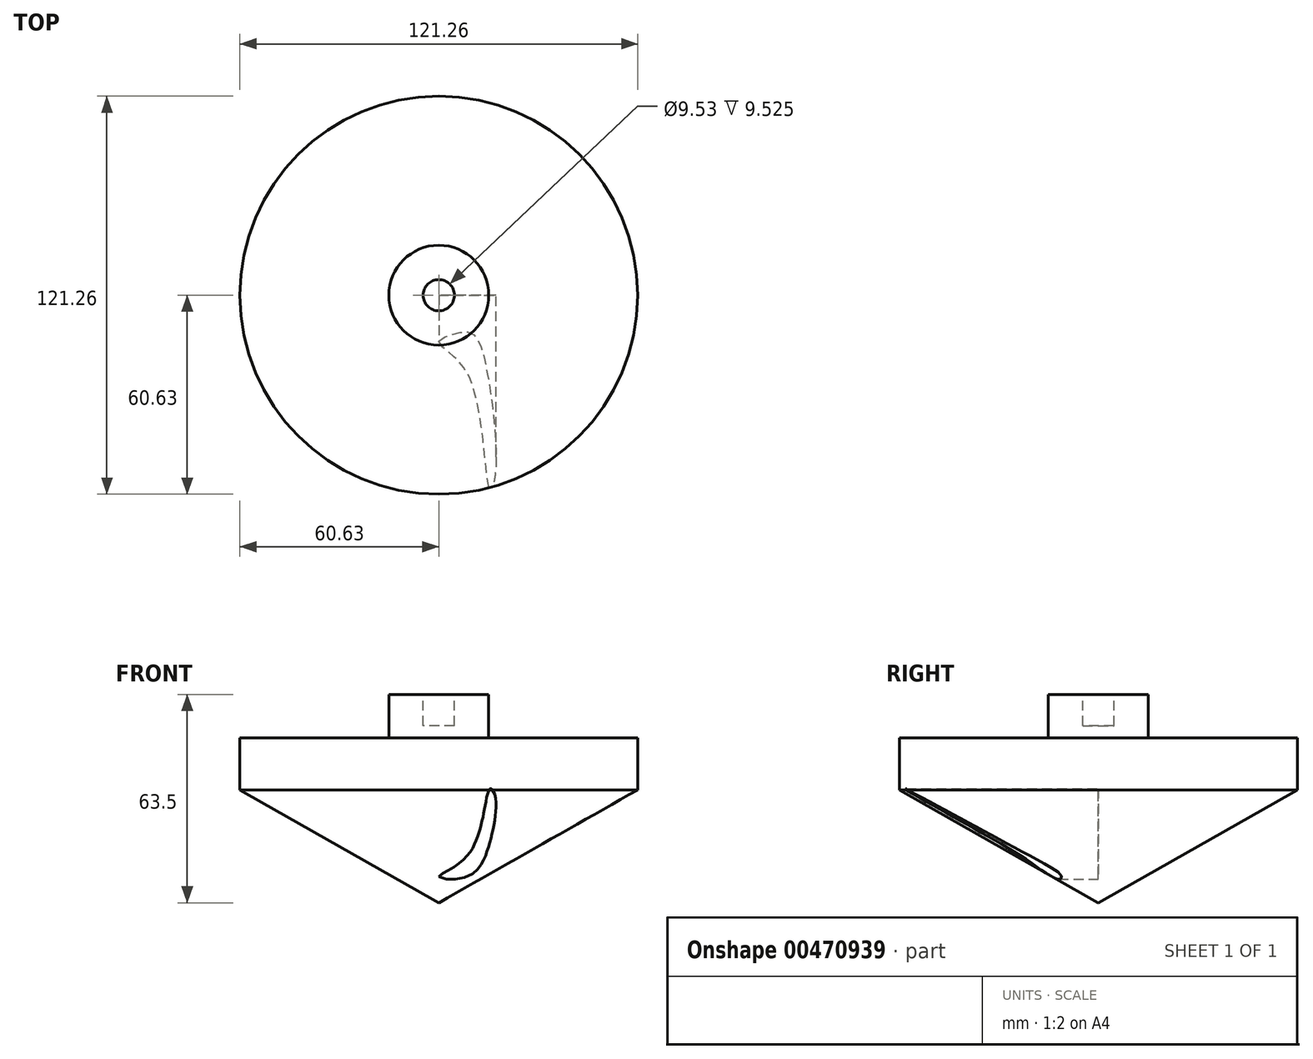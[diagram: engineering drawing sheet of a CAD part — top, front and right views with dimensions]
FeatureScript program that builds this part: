
annotation { "Feature Type Name" : "Feature", "Feature Type Description" : "" }
export const myFeature = defineFeature(function(context is Context, id is Id, definition is map)
    precondition{}
    {
        {
            var Q0;
            Q0=qCreatedBy(makeId("Front.planeOp"),FACE);
            var sketch = newSketch(context, id + "F0", { "sketchPlane" : qUnion([Q0])});
            skLineSegment(sketch, "E0", {"start": v(0, 0) * mm, "end": v(60.63, 34.42) * mm});
            skLineSegment(sketch, "E1", {"start": v(60.63, 34.42) * mm, "end": v(60.63, 50.2) * mm});
            skLineSegment(sketch, "E2", {"start": v(60.63, 50.2) * mm, "end": v(15.21, 50.2) * mm});
            skLineSegment(sketch, "E3", {"start": v(15.21, 50.2) * mm, "end": v(15.21, 63.5) * mm});
            skPoint(sketch, "E4.endSnap0", {"position": v(15.21, 56.85) * mm});
            skLineSegment(sketch, "E5", {"start": v(15.21, 63.5) * mm, "end": v(0, 63.5) * mm});
            skLineSegment(sketch, "E6", {"start": v(0, 0) * mm, "end": v(0, 63.5) * mm});
            skSolve(sketch);
        }
        {
            var Q0;
            Q0=makeQuery(id+"F0.imprint","IMPRINT",FACE,{"disambiguationData":[TD([[makeQuery(id+"F0.imprint","IMPRINT",EDGE,{"derivedFrom":sQuery(id+"F0.wireOp",EDGE,"E0")}),1.0]])]});
            var Q1;
            Q1=sQuery(id+"F0.wireOp",EDGE,"E6");
            revolve(context, id + "F1", {"entities" : qUnion([Q0]), "axis" : qUnion([Q1]), "revolveType" : RevolveType.FULL});
        }
        {
            var Q0;
            Q0=makeQuery(id+"F1.opRevolve","SWEPT_FACE",FACE,{"disambiguationData":[OSD([sQuery(id+"F0.wireOp",EDGE,"E5")])]});
            var sketch = newSketch(context, id + "F2", { "sketchPlane" : qUnion([Q0])});
            skCircle(sketch, "E7", {"center": v(0, 0) * mm, "radius": 4.76 * mm});
            skSolve(sketch);
        }
        {
            var Q0;
            Q0 = qSketchRegion(id + "F2", true);
            extrude(context, id + "F3", {"entities" : qUnion([Q0]), "operationType" : NewBodyOperationType.REMOVE, "oppositeDirection" : true, "depth" : 9.52 * mm});
        }
        {
            var Q0;
            Q0=qCreatedBy(makeId("Front.planeOp"),FACE);
            var sketch = newSketch(context, id + "F4", { "sketchPlane" : qUnion([Q0])});
            skLineSegment(sketch, "E8", {"start": v(0, 0) * mm, "end": v(0, 7.94) * mm});
            skLineSegment(sketch, "E9", {"start": v(0, 7.94) * mm, "end": v(0, 0) * mm});
            skFitSpline(sketch, "E10", {"points": [v(0, 7.94) * mm, v(9.32, 15.14) * mm, v(15.54, 34.68) * mm, v(17.18, 32.57) * mm, v(15.3, 17.55) * mm, v(8.5, 7.94) * mm, v(0, 7.94) * mm]});
            skSolve(sketch);
        }
        {
            var Q0;
            Q0 = qSketchRegion(id + "F4", true);
            extrude(context, id + "F5", {"entities" : qUnion([Q0]), "operationType" : NewBodyOperationType.REMOVE, "depth" : 76.2 * mm});
        }
    });
